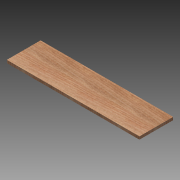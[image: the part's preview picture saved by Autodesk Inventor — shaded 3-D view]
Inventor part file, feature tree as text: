
AUTODESK INVENTOR PART (.ipt)
format: ipt  version: 2015 (Build 190159000, 159)  size: 86,528 bytes
history: native  units: in
note: dims shown in document units (in); Inventor stores cm internally (conversion verified against a paired STEP export)
features: extrude x1, sketch x1
ambient origin geometry x8: Origin, YZ Plane, XZ Plane, XY Plane, X Axis, Y Axis, Z Axis, Center Point
bodies: Solid1 (feature_tree)
feature tree (2):
  extrude  "Extrusion1"  Depth=27.5591in
  sketch  "Sketch1"  dims[d0=7.0079in d1=27.5591in d2=0.5906in d3=0.0in]
